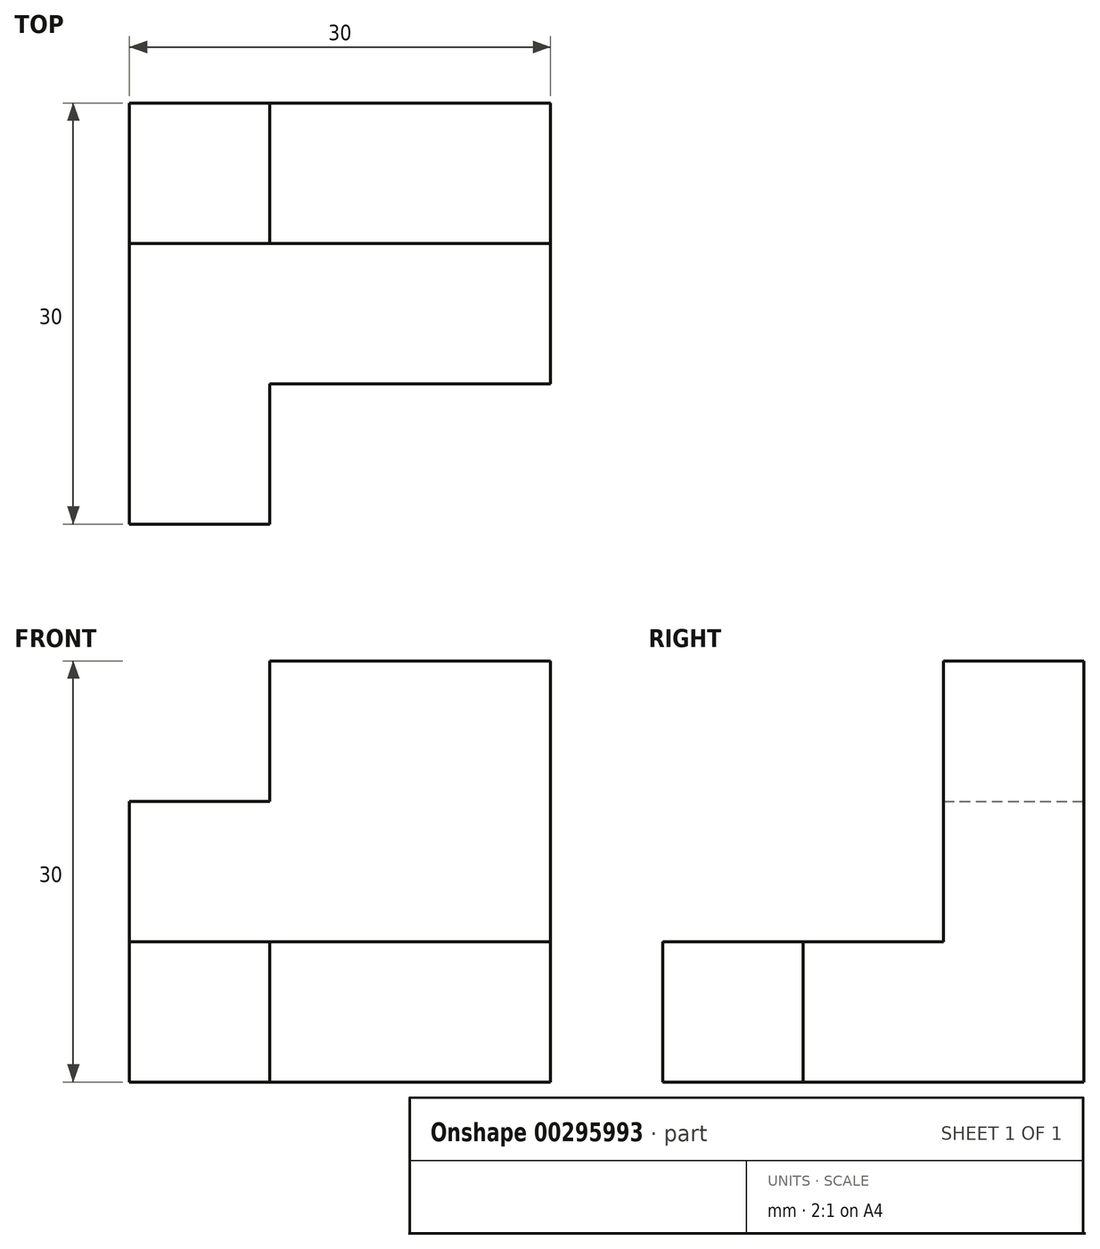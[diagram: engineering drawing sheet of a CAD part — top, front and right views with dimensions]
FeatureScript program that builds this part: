
annotation { "Feature Type Name" : "Feature", "Feature Type Description" : "" }
export const myFeature = defineFeature(function(context is Context, id is Id, definition is map)
    precondition{}
    {
        {
            var Q0;
            Q0=qCreatedBy(makeId("Top.planeOp"),FACE);
            var sketch = newSketch(context, id + "F0", { "sketchPlane" : qUnion([Q0])});
            skLineSegment(sketch, "E0", {"start": v(0, 0) * mm, "end": v(10, 0) * mm});
            skLineSegment(sketch, "E1", {"start": v(10, 0) * mm, "end": v(10, 10) * mm});
            skLineSegment(sketch, "E2", {"start": v(10, 10) * mm, "end": v(30, 10) * mm});
            skLineSegment(sketch, "E3", {"start": v(30, 10) * mm, "end": v(30, 30) * mm});
            skLineSegment(sketch, "E4", {"start": v(30, 30) * mm, "end": v(0, 30) * mm});
            skLineSegment(sketch, "E5", {"start": v(0, 30) * mm, "end": v(0, 0) * mm});
            skSolve(sketch);
        }
        {
            var Q0;
            Q0 = qSketchRegion(id + "F0", true);
            var Q1;
            Q1=makeQuery(id+"F0.imprint","IMPRINT",FACE,{"disambiguationData":[TD([[makeQuery(id+"F0.imprint","IMPRINT",EDGE,{"derivedFrom":sQuery(id+"F0.wireOp",EDGE,"E0")}),1.0]])]});
            extrude(context, id + "F1", {"entities" : qUnion([Q0, Q1]), "depth" : 10 * mm});
        }
        {
            var Q0;
            Q0=makeQuery(id+"F1.opExtrude","SWEPT_FACE",FACE,{"disambiguationData":[OSD([sQuery(id+"F0.wireOp",EDGE,"E4")])]});
            var sketch = newSketch(context, id + "F2", { "sketchPlane" : qUnion([Q0])});
            skLineSegment(sketch, "E6", {"start": v(-30, 0) * mm, "end": v(0, 0) * mm});
            skLineSegment(sketch, "E7", {"start": v(0, 0) * mm, "end": v(0, 20) * mm});
            skLineSegment(sketch, "E8", {"start": v(0, 20) * mm, "end": v(-10, 20) * mm});
            skLineSegment(sketch, "E9", {"start": v(-10, 20) * mm, "end": v(-10, 30) * mm});
            skLineSegment(sketch, "E10", {"start": v(-10, 30) * mm, "end": v(-30, 30) * mm});
            skLineSegment(sketch, "E11", {"start": v(-30, 30) * mm, "end": v(-30, 0) * mm});
            skSolve(sketch);
        }
        {
            var Q0;
            Q0 = qSketchRegion(id + "F2", true);
            var Q1;
            {var subQ1=sQuery(id+"F2.wireOp",EDGE,"E8");Q1=makeQuery(id+"F2.imprint","IMPRINT",FACE,{"disambiguationData":[TD([[makeQuery(id+"F2.imprint","IMPRINT",EDGE,{"derivedFrom":subQ1}),1.0]])]});}
            extrude(context, id + "F3", {"entities" : qUnion([Q0, Q1]), "operationType" : NewBodyOperationType.ADD, "oppositeDirection" : true, "depth" : 10 * mm});
        }
    });
